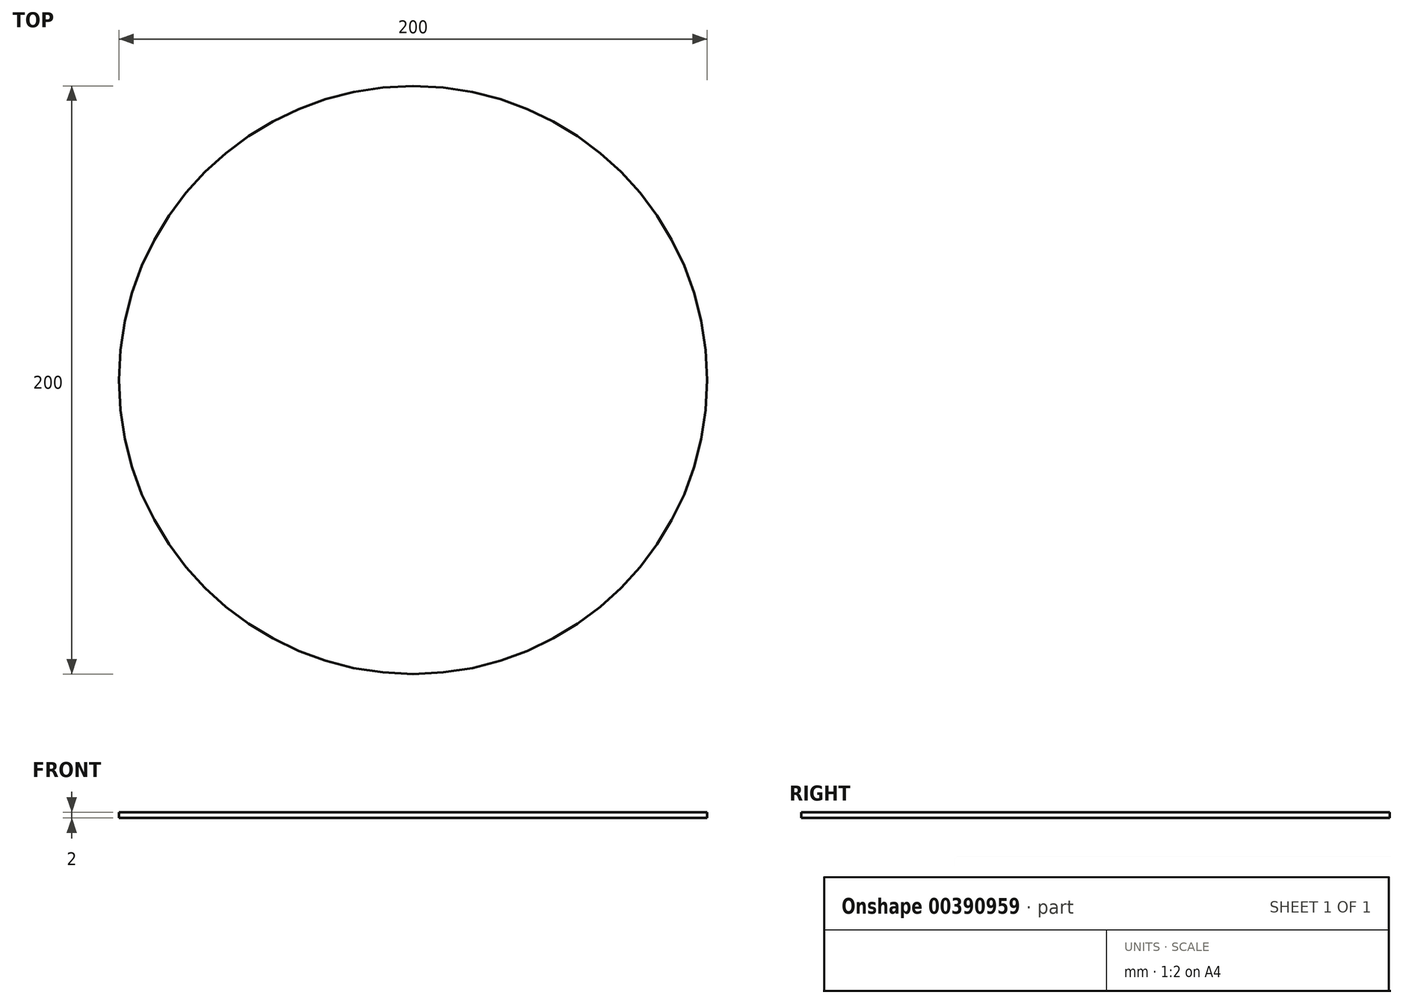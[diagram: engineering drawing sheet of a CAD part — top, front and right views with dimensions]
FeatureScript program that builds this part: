
annotation { "Feature Type Name" : "Feature", "Feature Type Description" : "" }
export const myFeature = defineFeature(function(context is Context, id is Id, definition is map)
    precondition{}
    {
        {
            var Q0;
            Q0=qCreatedBy(makeId("Top.planeOp"),FACE);
            var sketch = newSketch(context, id + "F0", { "sketchPlane" : qUnion([Q0])});
            skCircle(sketch, "E0", {"center": v(0, 0) * mm, "radius": 100 * mm});
            skSolve(sketch);
        }
        {
            var Q0;
            Q0=makeQuery(id+"F0.imprint","IMPRINT",FACE,{"disambiguationData":[TD([[makeQuery(id+"F0.imprint","IMPRINT",EDGE,{"derivedFrom":sQuery(id+"F0.wireOp",EDGE,"E0")}),1.0]])]});
            extrude(context, id + "F1", {"entities" : qUnion([Q0]), "depth" : 2 * mm, "offsetDistance" : 25 * mm});
        }
    });
